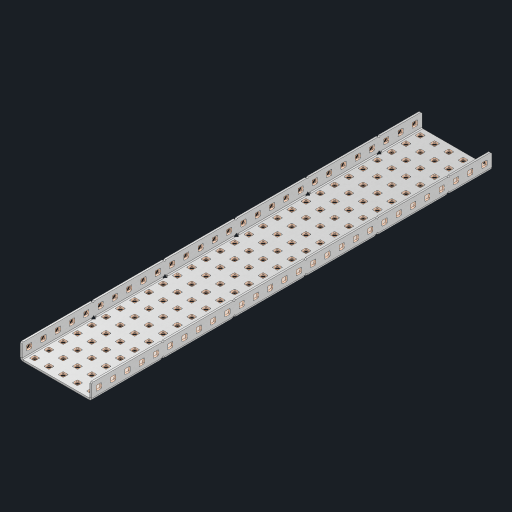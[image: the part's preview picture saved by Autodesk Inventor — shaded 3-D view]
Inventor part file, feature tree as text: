
AUTODESK INVENTOR PART (.ipt)
format: ipt  version: 2023 (Build 270158000, 158)  size: 2,150,400 bytes
history: native  units: in
note: dims shown in document units (in); Inventor stores cm internally (conversion verified against a paired STEP export)
features: other x201, extrude x195, sheet_metal_op x10, sketch x8, mirror x1, pattern_linear x1, chamfer x1
ambient origin geometry x8: Origin, YZ Plane, XZ Plane, XY Plane, X Axis, Y Axis, Z Axis, Center Point
bodies: Solid1 (feature_tree), Body (feature_tree)
feature tree (417):
  other  "Flange Pattern Plane"
  sheet_metal_op  "Flange Pattern"
  sheet_metal_op  "Body Pattern"
  other  "Arc Length"
  mirror  "Notch Mirror"
  pattern_linear  "Notch Pattern"  Spacing1=0.25in  [1 undecoded]
  chamfer  "End Chamfer"
  extrude  "Half Cut"  Depth=0.0625in
  sketch  "Sketch1"  dims[d0=2.5in]
  other  "Plate1"
  sketch  "Sketch2"  dims[d1=14.0in]
  other  "Plate2"
  sheet_metal_op  "Bend1"
  sheet_metal_op  "Corner1"
  sketch  "Sketch3"  dims[d2=0.0625in]
  other  "Flange Pattern Sketch"
  sketch  "Sketch7"  dims[d3=0.0625in]
  other  "Srf1"
  other  "Srf2"
  sketch  "Sketch8"  dims[d4=0.0312in]
  sketch  "Sketch9"  dims[d5=0.125in]
  other  "Srf91"
  sheet_metal_op  "Body Pattern Sketch"
  other  "Srf92"
  sketch  "Sketch13"  dims[d6=0.0625in]
  sketch  "Sketch14"  dims[d7=0.5in d8=90.0deg d9=0.0312in d10=0.25in d11=0.0625in d12=0.0625in d16=0.182in d17=0.02in d18=0.0625in d19=0.0in d20=0.25in d21=0.25in d46=0.172in d47=1.0in d48=0.0in d49=0.182in d50=0.02in d51=0.25in d52=0.25in d53=0.0625in d54=0.0in d55=0.172in d56=1.0in d57=0.0in d60=11.0236in d62=0.5in d63=1.9685in d65=0.5in d85=0.1473in d86=0.1782in d88=0.04in d89=0.0625in d90=0.0in d91=0.04in d92=0.0491in d95=2.5in d96=0.04in d97=0.25in d98=45.0deg d101=0.0in d102=2.497in d131=2.5in d132=11.0236in d134=0.5in d139=0.5in]
  other  "Srf856"
  other  "Srf1310"
  other  "Srf1311"
  other  "Srf1312"
  other  "Srf1376"
  other  "Srf1377"
  other  "Srf1728"
  other  "Srf1755"
  other  "Srf1878"
  other  "Srf1879"
  other  "Srf1880"
  other  "Srf1881"
  other  "Srf1882"
  other  "Srf1883"
  other  "Srf1884"
  other  "Srf1885"
  other  "Srf1886"
  other  "Srf1887"
  other  "Srf1888"
  other  "Srf1889"
  other  "Srf1890"
  other  "Srf1891"
  other  "Srf1892"
  other  "Srf1893"
  other  "Srf1894"
  other  "Srf1895"
  other  "Srf1896"
  other  "Srf1897"
  other  "Srf1898"
  other  "Srf1899"
  other  "Srf1900"
  other  "Srf1901"
  other  "Srf1902"
  other  "Srf1903"
  other  "Srf1904"
  other  "Srf1905"
  other  "Srf1906"
  other  "Srf1942"
  other  "Srf1943"
  other  "Srf1944"
  other  "Srf1945"
  other  "Srf1946"
  other  "Srf1947"
  other  "Srf1948"
  other  "Srf1949"
  other  "Srf1950"
  other  "Srf1951"
  other  "Srf1952"
  other  "Srf1953"
  other  "Srf1954"
  other  "Srf1955"
  other  "Srf1956"
  other  "Srf1957"
  other  "Srf1958"
  other  "Srf1959"
  other  "Srf1960"
  other  "Srf1961"
  other  "Srf1962"
  other  "Srf1963"
  other  "Srf1964"
  other  "Srf1965"
  other  "Srf1966"
  other  "Srf1967"
  other  "Srf1968"
  other  "Srf1969"
  other  "Srf1970"
  other  "Srf2111"
  other  "Srf2112"
  other  "Srf2113"
  other  "Srf2114"
  other  "Srf2115"
  other  "Srf2116"
  other  "Srf2117"
  other  "Srf2118"
  other  "Srf2119"
  other  "Srf2120"
  other  "Srf2121"
  other  "Srf2122"
  other  "Srf2123"
  other  "Srf2124"
  other  "Srf2125"
  other  "Srf2126"
  other  "Srf2127"
  other  "Srf2128"
  other  "Srf2129"
  other  "Srf2130"
  other  "Srf2131"
  other  "Srf2146"
  other  "Srf2147"
  other  "Srf2148"
  other  "Srf2149"
  other  "Srf2150"
  other  "Srf2151"
  other  "Srf2152"
  other  "Srf2153"
  other  "Srf2154"
  other  "Srf2155"
  other  "Srf2156"
  other  "Srf2157"
  other  "Srf2158"
  other  "Srf2159"
  other  "Srf2160"
  other  "Srf2161"
  other  "Srf2162"
  other  "Srf2163"
  other  "Srf2164"
  other  "Srf2165"
  other  "Srf2166"
  other  "Srf2167"
  other  "Srf2168"
  other  "Srf2169"
  other  "Srf2170"
  other  "Srf2171"
  other  "Srf2172"
  other  "Srf2173"
  other  "Srf2174"
  other  "Srf2175"
  other  "Srf2176"
  other  "Srf2177"
  other  "Srf2178"
  other  "Srf2179"
  other  "Srf2180"
  other  "Srf2181"
  other  "Srf2182"
  other  "Srf2183"
  other  "Srf2184"
  other  "Srf2185"
  other  "Srf2186"
  other  "Srf2187"
  other  "Srf2188"
  other  "Srf2189"
  other  "Srf2190"
  other  "Srf2191"
  other  "Srf2192"
  other  "Srf2193"
  other  "Srf2194"
  other  "Srf2195"
  other  "Srf2196"
  other  "Srf2197"
  other  "Srf2198"
  other  "Srf2199"
  other  "Srf2200"
  other  "Srf2201"
  other  "Srf2202"
  other  "Srf2203"
  other  "Srf2204"
  other  "Srf2205"
  other  "Srf2206"
  other  "Srf2207"
  other  "Srf2208"
  other  "Srf2209"
  other  "Srf2210"
  other  "Srf2211"
  other  "Srf2212"
  other  "Srf2213"
  other  "Srf2214"
  other  "Srf2215"
  other  "Srf2216"
  other  "Srf2217"
  other  "Srf2218"
  other  "Srf2219"
  other  "Srf2220"
  other  "Srf2221"
  other  "Srf2222"
  other  "Srf2223"
  other  "Srf2224"
  other  "Srf2225"
  other  "Srf2226"
  other  "Srf2227"
  other  "Srf2228"
  other  "Srf2229"
  other  "Srf2230"
  other  "Srf2231"
  other  "Srf2232"
  other  "Srf2233"
  other  "Srf2234"
  other  "Srf2235"
  other  "Srf2236"
  other  "Srf2237"
  other  "Srf2238"
  other  "Srf2239"
  other  "Srf2240"
  other  "Srf2241"
  other  "Srf2242"
  other  "Srf2243"
  other  "Srf2244"
  other  "Srf2245"
  other  "Srf2246"
  other  "Srf2247"
  other  "Srf2248"
  other  "Srf2249"
  other  "Srf2250"
  sheet_metal_op  "Flange Stamp"
  sheet_metal_op  "Flange Circle"
  sheet_metal_op  "Body Stamp"
  sheet_metal_op  "Body Circle"
  sheet_metal_op  "Notch"
  extrude  "ExtrusionSrf2"  Depth=0.0625in
  extrude  "ExtrusionSrf92"  Depth=2.5in
  extrude  "ExtrusionSrf856"  Depth=0.02in
  extrude  "ExtrusionSrf1310"  Depth=0.0625in
  extrude  "ExtrusionSrf1311"  TaperAngle=0.0deg  [1 undecoded]
  extrude  "ExtrusionSrf1312"  Depth=0.25in
  extrude  "ExtrusionSrf1376"  Depth=0.25in
  extrude  "ExtrusionSrf1377"  Depth=2.5in
  extrude  "ExtrusionSrf1728"  Depth=2.5in TaperAngle=0.0deg
  extrude  "ExtrusionSrf1755"  Depth=2.5in
  extrude  "ExtrusionSrf1878"  Depth=0.02in
  extrude  "ExtrusionSrf1879"  Depth=0.25in
  extrude  "ExtrusionSrf1880"  Depth=0.25in
  extrude  "ExtrusionSrf1881"  Depth=0.0625in
  extrude  "ExtrusionSrf1882"  TaperAngle=0.0deg  [1 undecoded]
  extrude  "ExtrusionSrf1883"  Depth=2.5in
  extrude  "ExtrusionSrf1884"  Depth=2.5in TaperAngle=0.0deg
  extrude  "ExtrusionSrf1885"  Depth=2.5in
  extrude  "ExtrusionSrf1886"  Depth=2.5in
  extrude  "ExtrusionSrf1887"  Depth=2.5in
  extrude  "ExtrusionSrf1888"  Depth=2.5in
  extrude  "ExtrusionSrf1889"  Depth=2.5in
  extrude  "ExtrusionSrf1890"  Depth=0.0625in
  extrude  "ExtrusionSrf1891"  TaperAngle=0.0deg  [1 undecoded]
  extrude  "ExtrusionSrf1892"  Depth=2.5in
  extrude  "ExtrusionSrf1893"  Depth=2.5in
  extrude  "ExtrusionSrf1894"  Depth=2.5in
  extrude  "ExtrusionSrf1895"  Depth=0.25in TaperAngle=45.0deg
  extrude  "ExtrusionSrf1896"  TaperAngle=0.0deg  [1 undecoded]
  extrude  "ExtrusionSrf1897"  Depth=2.5in
  extrude  "ExtrusionSrf1898"  Depth=2.5in
  extrude  "ExtrusionSrf1899"  Depth=2.5in
  extrude  "ExtrusionSrf1900"  Depth=2.5in
  extrude  "ExtrusionSrf1901"  Depth=2.5in
  extrude  "ExtrusionSrf1902"  [1 undecoded]
  extrude  "ExtrusionSrf1903"  [1 undecoded]
  extrude  "ExtrusionSrf1904"  [1 undecoded]
  extrude  "ExtrusionSrf1905"  [1 undecoded]
  extrude  "ExtrusionSrf1906"  [1 undecoded]
  extrude  "ExtrusionSrf1942"  [1 undecoded]
  extrude  "ExtrusionSrf1943"  [1 undecoded]
  extrude  "ExtrusionSrf1944"  [1 undecoded]
  extrude  "ExtrusionSrf1945"  [1 undecoded]
  extrude  "ExtrusionSrf1946"  [1 undecoded]
  extrude  "ExtrusionSrf1947"  [1 undecoded]
  extrude  "ExtrusionSrf1948"  [1 undecoded]
  extrude  "ExtrusionSrf1949"  [1 undecoded]
  extrude  "ExtrusionSrf1950"  [1 undecoded]
  extrude  "ExtrusionSrf1951"  [1 undecoded]
  extrude  "ExtrusionSrf1952"  [1 undecoded]
  extrude  "ExtrusionSrf1953"  [1 undecoded]
  extrude  "ExtrusionSrf1954"  [1 undecoded]
  extrude  "ExtrusionSrf1955"  [1 undecoded]
  extrude  "ExtrusionSrf1956"  [1 undecoded]
  extrude  "ExtrusionSrf1957"  [1 undecoded]
  extrude  "ExtrusionSrf1958"  [1 undecoded]
  extrude  "ExtrusionSrf1959"  [1 undecoded]
  extrude  "ExtrusionSrf1960"  [1 undecoded]
  extrude  "ExtrusionSrf1961"  [1 undecoded]
  extrude  "ExtrusionSrf1962"  [1 undecoded]
  extrude  "ExtrusionSrf1963"  [1 undecoded]
  extrude  "ExtrusionSrf1964"  [1 undecoded]
  extrude  "ExtrusionSrf1965"  [1 undecoded]
  extrude  "ExtrusionSrf1966"  [1 undecoded]
  extrude  "ExtrusionSrf1967"  [1 undecoded]
  extrude  "ExtrusionSrf1968"  [1 undecoded]
  extrude  "ExtrusionSrf1969"  [1 undecoded]
  extrude  "ExtrusionSrf1970"  [1 undecoded]
  extrude  "ExtrusionSrf2111"  [1 undecoded]
  extrude  "ExtrusionSrf2112"  [1 undecoded]
  extrude  "ExtrusionSrf2113"  [1 undecoded]
  extrude  "ExtrusionSrf2114"  [1 undecoded]
  extrude  "ExtrusionSrf2115"  [1 undecoded]
  extrude  "ExtrusionSrf2116"  [1 undecoded]
  extrude  "ExtrusionSrf2117"  [1 undecoded]
  extrude  "ExtrusionSrf2118"  [1 undecoded]
  extrude  "ExtrusionSrf2119"  [1 undecoded]
  extrude  "ExtrusionSrf2120"  [1 undecoded]
  extrude  "ExtrusionSrf2121"  [1 undecoded]
  extrude  "ExtrusionSrf2122"  [1 undecoded]
  extrude  "ExtrusionSrf2123"  [1 undecoded]
  extrude  "ExtrusionSrf2124"  [1 undecoded]
  extrude  "ExtrusionSrf2125"  [1 undecoded]
  extrude  "ExtrusionSrf2126"  [1 undecoded]
  extrude  "ExtrusionSrf2127"  [1 undecoded]
  extrude  "ExtrusionSrf2128"  [1 undecoded]
  extrude  "ExtrusionSrf2129"  [1 undecoded]
  extrude  "ExtrusionSrf2130"  [1 undecoded]
  extrude  "ExtrusionSrf2131"  [1 undecoded]
  extrude  "ExtrusionSrf2146"  [1 undecoded]
  extrude  "ExtrusionSrf2147"  [1 undecoded]
  extrude  "ExtrusionSrf2148"  [1 undecoded]
  extrude  "ExtrusionSrf2149"  [1 undecoded]
  extrude  "ExtrusionSrf2150"  [1 undecoded]
  extrude  "ExtrusionSrf2151"  [1 undecoded]
  extrude  "ExtrusionSrf2152"  [1 undecoded]
  extrude  "ExtrusionSrf2153"  [1 undecoded]
  extrude  "ExtrusionSrf2154"  [1 undecoded]
  extrude  "ExtrusionSrf2155"  [1 undecoded]
  extrude  "ExtrusionSrf2156"  [1 undecoded]
  extrude  "ExtrusionSrf2157"  [1 undecoded]
  extrude  "ExtrusionSrf2158"  [1 undecoded]
  extrude  "ExtrusionSrf2159"  [1 undecoded]
  extrude  "ExtrusionSrf2160"  [1 undecoded]
  extrude  "ExtrusionSrf2161"  [1 undecoded]
  extrude  "ExtrusionSrf2162"  [1 undecoded]
  extrude  "ExtrusionSrf2163"  [1 undecoded]
  extrude  "ExtrusionSrf2164"  [1 undecoded]
  extrude  "ExtrusionSrf2165"  [1 undecoded]
  extrude  "ExtrusionSrf2166"  [1 undecoded]
  extrude  "ExtrusionSrf2167"  [1 undecoded]
  extrude  "ExtrusionSrf2168"  [1 undecoded]
  extrude  "ExtrusionSrf2169"  [1 undecoded]
  extrude  "ExtrusionSrf2170"  [1 undecoded]
  extrude  "ExtrusionSrf2171"  [1 undecoded]
  extrude  "ExtrusionSrf2172"  [1 undecoded]
  extrude  "ExtrusionSrf2173"  [1 undecoded]
  extrude  "ExtrusionSrf2174"  [1 undecoded]
  extrude  "ExtrusionSrf2175"  [1 undecoded]
  extrude  "ExtrusionSrf2176"  [1 undecoded]
  extrude  "ExtrusionSrf2177"  [1 undecoded]
  extrude  "ExtrusionSrf2178"  [1 undecoded]
  extrude  "ExtrusionSrf2179"  [1 undecoded]
  extrude  "ExtrusionSrf2180"  [1 undecoded]
  extrude  "ExtrusionSrf2181"  [1 undecoded]
  extrude  "ExtrusionSrf2182"  [1 undecoded]
  extrude  "ExtrusionSrf2183"  [1 undecoded]
  extrude  "ExtrusionSrf2184"  [1 undecoded]
  extrude  "ExtrusionSrf2185"  [1 undecoded]
  extrude  "ExtrusionSrf2186"  [1 undecoded]
  extrude  "ExtrusionSrf2187"  [1 undecoded]
  extrude  "ExtrusionSrf2188"  [1 undecoded]
  extrude  "ExtrusionSrf2189"  [1 undecoded]
  extrude  "ExtrusionSrf2190"  [1 undecoded]
  extrude  "ExtrusionSrf2191"  [1 undecoded]
  extrude  "ExtrusionSrf2192"  [1 undecoded]
  extrude  "ExtrusionSrf2193"  [1 undecoded]
  extrude  "ExtrusionSrf2194"  [1 undecoded]
  extrude  "ExtrusionSrf2195"  [1 undecoded]
  extrude  "ExtrusionSrf2196"  [1 undecoded]
  extrude  "ExtrusionSrf2197"  [1 undecoded]
  extrude  "ExtrusionSrf2198"  [1 undecoded]
  extrude  "ExtrusionSrf2199"  [1 undecoded]
  extrude  "ExtrusionSrf2200"  [1 undecoded]
  extrude  "ExtrusionSrf2201"  [1 undecoded]
  extrude  "ExtrusionSrf2202"  [1 undecoded]
  extrude  "ExtrusionSrf2203"  [1 undecoded]
  extrude  "ExtrusionSrf2204"  [1 undecoded]
  extrude  "ExtrusionSrf2205"  [1 undecoded]
  extrude  "ExtrusionSrf2206"  [1 undecoded]
  extrude  "ExtrusionSrf2207"  [1 undecoded]
  extrude  "ExtrusionSrf2208"  [1 undecoded]
  extrude  "ExtrusionSrf2209"  [1 undecoded]
  extrude  "ExtrusionSrf2210"  [1 undecoded]
  extrude  "ExtrusionSrf2211"  [1 undecoded]
  extrude  "ExtrusionSrf2212"  [1 undecoded]
  extrude  "ExtrusionSrf2213"  [1 undecoded]
  extrude  "ExtrusionSrf2214"  [1 undecoded]
  extrude  "ExtrusionSrf2215"  [1 undecoded]
  extrude  "ExtrusionSrf2216"  [1 undecoded]
  extrude  "ExtrusionSrf2217"  [1 undecoded]
  extrude  "ExtrusionSrf2218"  [1 undecoded]
  extrude  "ExtrusionSrf2219"  [1 undecoded]
  extrude  "ExtrusionSrf2220"  [1 undecoded]
  extrude  "ExtrusionSrf2221"  [1 undecoded]
  extrude  "ExtrusionSrf2222"  [1 undecoded]
  extrude  "ExtrusionSrf2223"  [1 undecoded]
  extrude  "ExtrusionSrf2224"  [1 undecoded]
  extrude  "ExtrusionSrf2225"  [1 undecoded]
  extrude  "ExtrusionSrf2226"  [1 undecoded]
  extrude  "ExtrusionSrf2227"  [1 undecoded]
  extrude  "ExtrusionSrf2228"  [1 undecoded]
  extrude  "ExtrusionSrf2229"  [1 undecoded]
  extrude  "ExtrusionSrf2230"  [1 undecoded]
  extrude  "ExtrusionSrf2231"  [1 undecoded]
  extrude  "ExtrusionSrf2232"  [1 undecoded]
  extrude  "ExtrusionSrf2233"  [1 undecoded]
  extrude  "ExtrusionSrf2234"  [1 undecoded]
  extrude  "ExtrusionSrf2235"  [1 undecoded]
  extrude  "ExtrusionSrf2236"  [1 undecoded]
  extrude  "ExtrusionSrf2237"  [1 undecoded]
  extrude  "ExtrusionSrf2238"  [1 undecoded]
  extrude  "ExtrusionSrf2239"  [1 undecoded]
  extrude  "ExtrusionSrf2240"  [1 undecoded]
  extrude  "ExtrusionSrf2241"  [1 undecoded]
  extrude  "ExtrusionSrf2242"  [1 undecoded]
  extrude  "ExtrusionSrf2243"  [1 undecoded]
  extrude  "ExtrusionSrf2244"  [1 undecoded]
  extrude  "ExtrusionSrf2245"  [1 undecoded]
  extrude  "ExtrusionSrf2246"  [1 undecoded]
  extrude  "ExtrusionSrf2247"  [1 undecoded]
  extrude  "ExtrusionSrf2248"  [1 undecoded]
  extrude  "ExtrusionSrf2249"  [1 undecoded]
  extrude  "ExtrusionSrf2250"  [1 undecoded]
note: 165 required parameter values undecoded (feature->parameter linkage not recoverable at this tier; creation-order binding heuristic only, values carry confidence <= 0.55)
